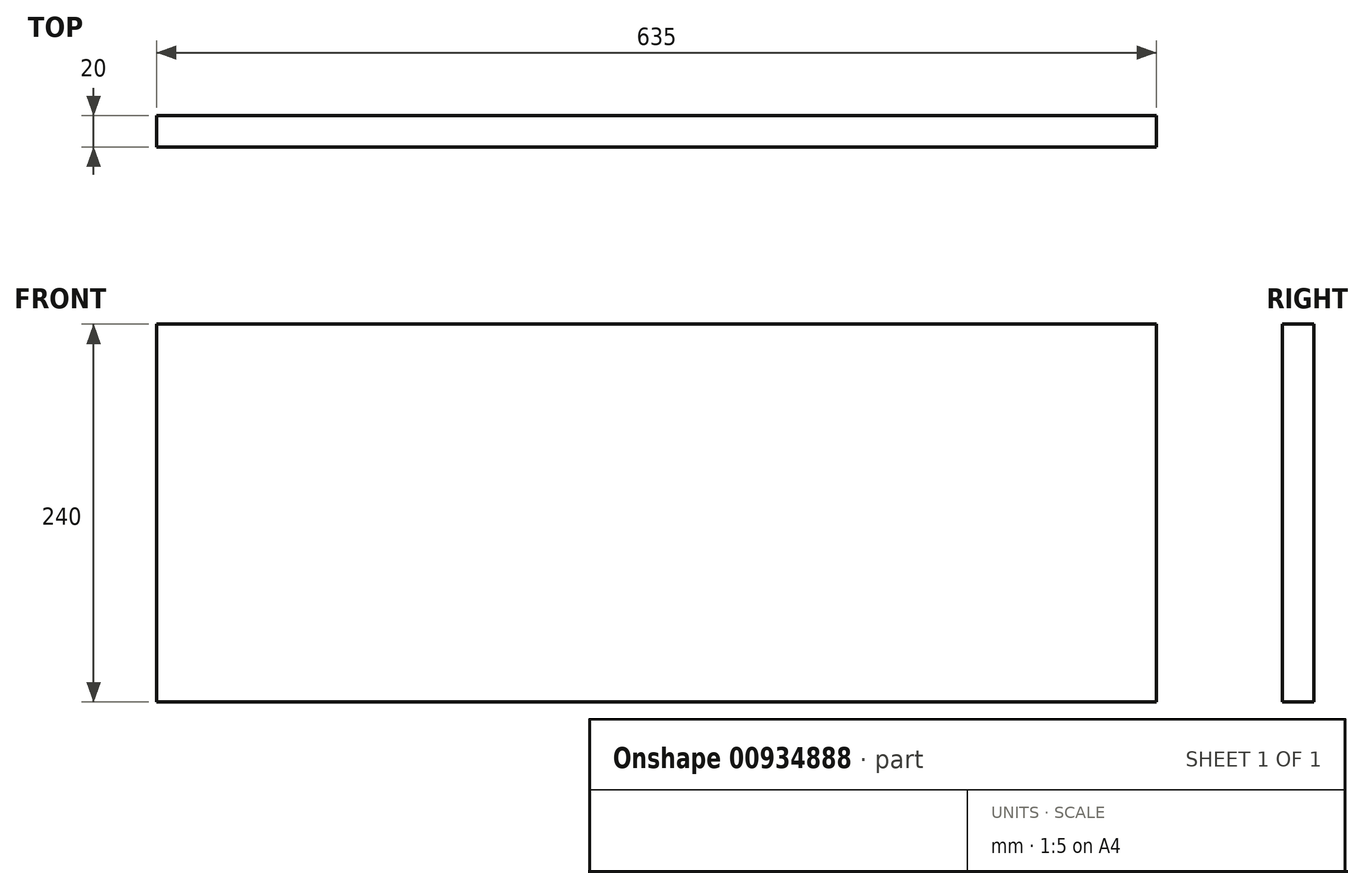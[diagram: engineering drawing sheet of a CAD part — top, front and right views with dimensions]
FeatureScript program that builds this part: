
annotation { "Feature Type Name" : "Feature", "Feature Type Description" : "" }
export const myFeature = defineFeature(function(context is Context, id is Id, definition is map)
    precondition{}
    {
        {
            var Q0;
            Q0=qCreatedBy(makeId("Front.planeOp"),FACE);
            var sketch = newSketch(context, id + "F0", { "sketchPlane" : qUnion([Q0])});
            skLineSegment(sketch, "E0.bottom", {"start": v(-635, 240) * mm, "end": v(0, 240) * mm});
            skLineSegment(sketch, "E0.top", {"start": v(-635, 0) * mm, "end": v(0, 0) * mm});
            skLineSegment(sketch, "E0.left", {"start": v(-635, 240) * mm, "end": v(-635, 0) * mm});
            skLineSegment(sketch, "E0.right", {"start": v(0, 240) * mm, "end": v(0, 0) * mm});
            skSolve(sketch);
        }
        {
            var Q0;
            Q0=makeQuery(id+"F0.imprint","IMPRINT",FACE,{"disambiguationData":[TD([[makeQuery(id+"F0.imprint","IMPRINT",EDGE,{"derivedFrom":sQuery(id+"F0.wireOp",EDGE,"E0.bottom")}),-1.0]])]});
            extrude(context, id + "F1", {"entities" : qUnion([Q0]), "depth" : 20 * mm, "offsetDistance" : 25 * mm});
        }
    });
